# Revit family: 1PRD_FrankeWS_UrnlFlshngVlvs_ElectronicUrinalFlushingSystems_AQUA420,AQUA422
name_source: partatom
category: Pipe Accessories
revit_build: Autodesk Revit 2015 (Build: 20160512_1515(x64)
units: mm (PartAtom-declared; Revit-internal decimal feet)

## types (2) — shared parameters
AssetType = Fixed
Category = Pr_40_20_93_79, Urinal flushing valves
DurationUnit = year
FlushValveMaterial = <By Category>
FlushVolume = 0.30 liter per second
FlushingRate = 0.0 L/s
GrossWeight = 1.50 kg
HasIntegralShutOffDevice = Yes
IfcExportAs = IfcValveType
IfcExportType = FLUSHING
IsHighPressure = No
Manufacturer = FRANKE Water Systems AG
ManufacturerName = FRANKE Water Systems AG
ManufacturerURL = www.franke.com
NBSDescription = Flush control devices
NBSReference = 90-15-35/470
NetWeight = 1.43 kg
OperatingControl = electronic self-closing
ProductInformation = http://igh.franke.mycontent.ch
URL = www.franke.com
Uniclass2015Code = Pr_75_50_46_31
Uniclass2015Title = Flush control devices
Uniclass2015Version = Products v1.7
Version = 1
WarrantyDurationUnit = year
zero-valued in all types: NominalHeight, NominalLength, NominalWidth

## per-type parameters (varying)
| type | BIMObjectName | Description | ModelNumber | Name |
| AQUA420 | PRD_FrankeWS_UrinalFlushingValves_ElectronicUrinalFlushingSystems_AQUA420 | Electronic siphon control unit for invisible installation. For touch free flushing of Franke stainless steel urinals. With flexible pressure hose, solenoid valve, electronic module and siphon with outside mounted sensor without water contact, hygiene flushing 24 h after the last activity, 230 V AC. | 2000071169 | Electronic urinal flushing systems AQUA420 |
| AQUA422 | PRD_FrankeWS_UrinalFlushingValves_ElectronicUrinalFlushingSystems_AQUA422 | Electronic siphon control unit for invisible installation. For touch free flushing of Franke stainless steel urinals. With flexible pressure hose, solenoid valve, electronic module and siphon with outside mounted sensor without water contact, hygiene flushing 24 h after the last activity, 230 V AC. for Franke slab urinals | 2000102700 | Electronic urinal flushing systems AQUA422 |

note: column(s) folded — value = type name in every type: Model, ModelReference

## geometry (parser evidence)
native form markers: Sweep x3
no freeform markers — native parametric forms only
